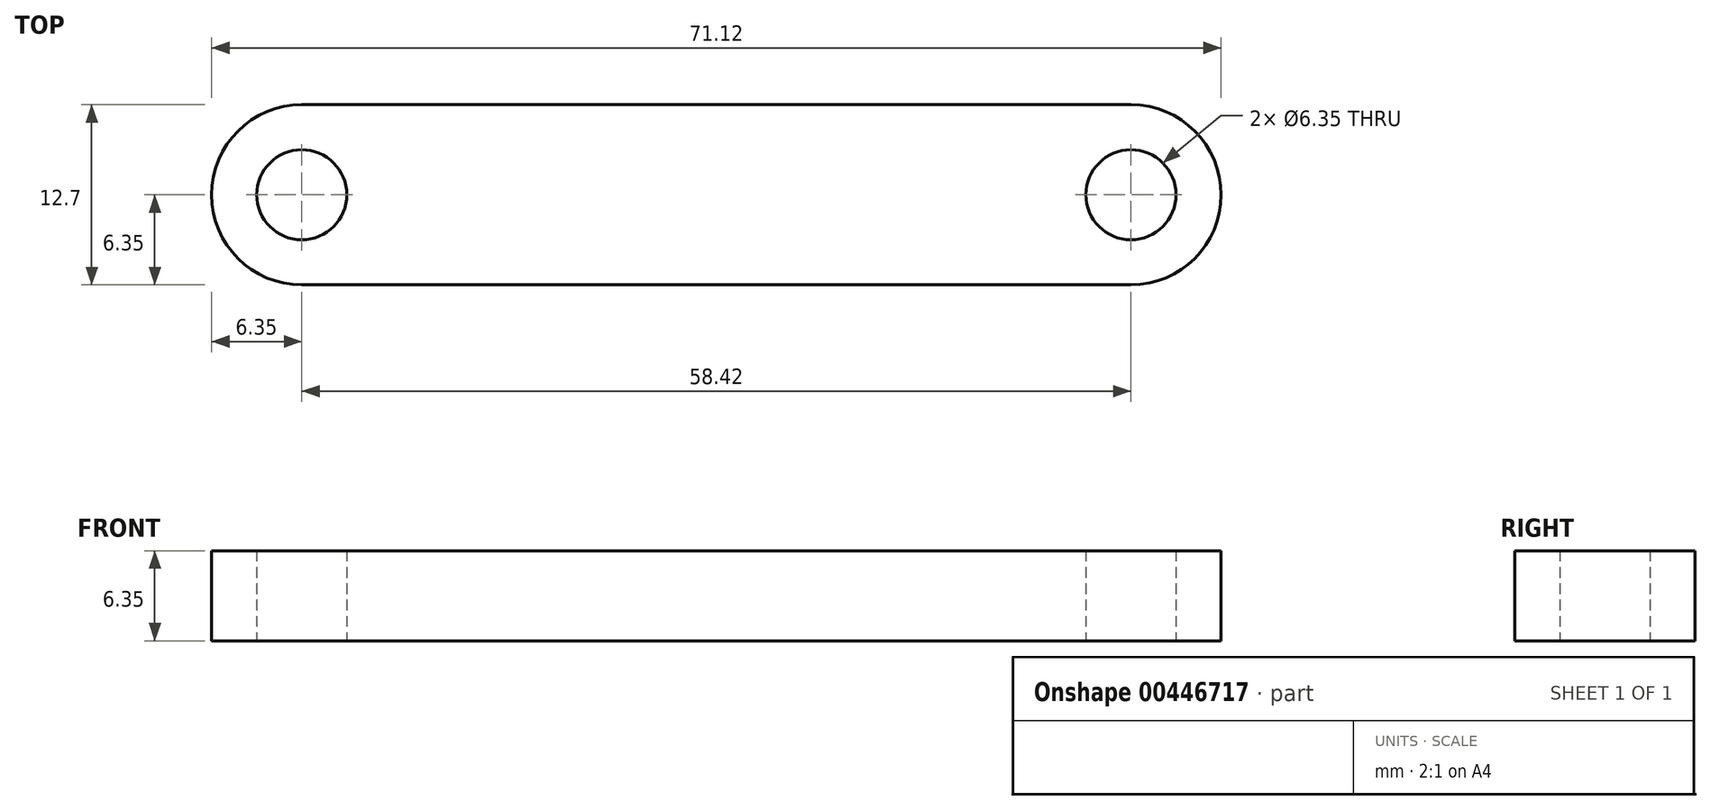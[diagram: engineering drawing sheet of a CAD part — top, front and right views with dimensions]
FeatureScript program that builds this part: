
annotation { "Feature Type Name" : "Feature", "Feature Type Description" : "" }
export const myFeature = defineFeature(function(context is Context, id is Id, definition is map)
    precondition{}
    {
        {
            var Q0;
            Q0=qCreatedBy(makeId("Top.planeOp"),FACE);
            var sketch = newSketch(context, id + "F0", { "sketchPlane" : qUnion([Q0])});
            skArc(sketch, "E0", {"start": v(-29.21, 6.35) * mm, "mid": v(-35.56, 0) * mm, "end": v(-29.21, -6.35) * mm});
            skArc(sketch, "E1", {"start": v(29.21, -6.35) * mm, "mid": v(35.56, 0) * mm, "end": v(29.21, 6.35) * mm});
            skCircle(sketch, "E2", {"center": v(-29.21, 0) * mm, "radius": 3.18 * mm});
            skCircle(sketch, "E3", {"center": v(29.21, 0) * mm, "radius": 3.18 * mm});
            skLineSegment(sketch, "E4", {"start": v(-29.21, 6.35) * mm, "end": v(29.21, 6.35) * mm});
            skLineSegment(sketch, "E5", {"start": v(-29.21, -6.35) * mm, "end": v(29.21, -6.35) * mm});
            skSolve(sketch);
        }
        {
            var Q0;
            Q0=makeQuery(id+"F0.imprint","IMPRINT",FACE,{"disambiguationData":[TD([[makeQuery(id+"F0.imprint","IMPRINT",EDGE,{"derivedFrom":sQuery(id+"F0.wireOp",EDGE,"E0")}),1.0]])]});
            extrude(context, id + "F1", {"entities" : qUnion([Q0]), "depth" : 6.35 * mm});
        }
    });
